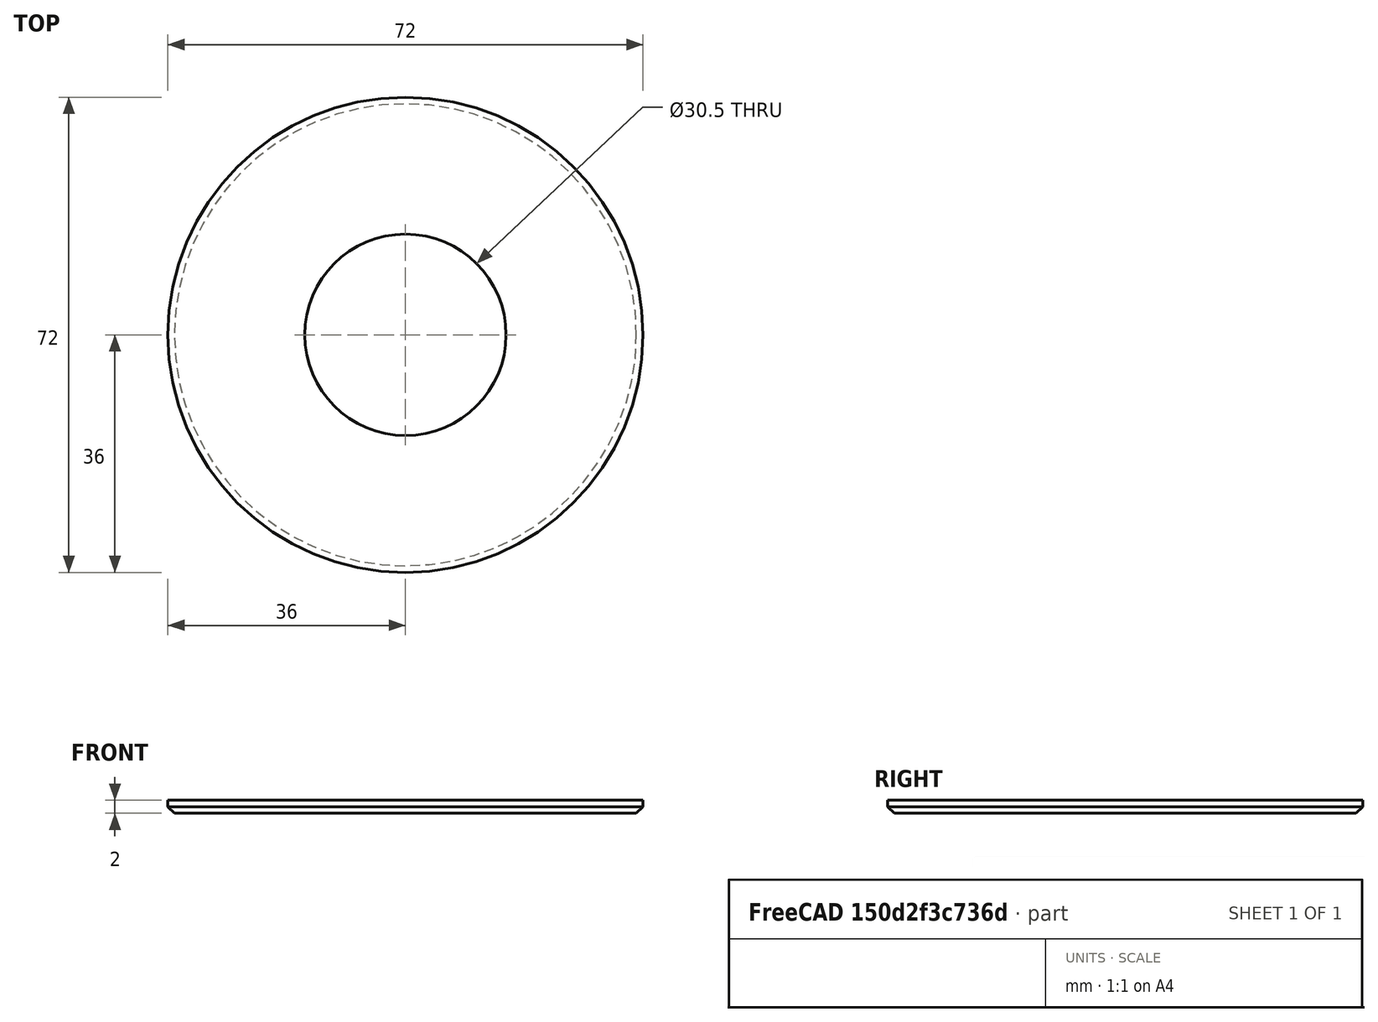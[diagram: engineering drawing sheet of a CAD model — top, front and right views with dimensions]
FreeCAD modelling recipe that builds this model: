
FCSTD DOCUMENT  (FreeCAD 0.18R16146 (Git))
Label: vp4013
License: All rights reserved
LicenseURL: http://en.wikipedia.org/wiki/All_rights_reserved
objects: Sketcher::SketchObject×1, PartDesign::Pad×1, PartDesign::Chamfer×1, PartDesign::Body×1
note: 5 computed .brp shape members not serialized (recipe doc carries the construction recipe); baked Part::Feature solids carry a one-line shape summary decoded from their .brp

FEATURE [Sketcher::SketchObject] Sketch
  MapMode = 5
  Support = -> [XY_Plane]
  sketch-geometry (2):
    g0: Circle CenterX=0 CenterY=0 CenterZ=0 NormalX=0 NormalY=0 NormalZ=1 AngleXU=0 Radius=15.25
    g1: Circle CenterX=0 CenterY=0 CenterZ=0 NormalX=0 NormalY=0 NormalZ=1 AngleXU=0 Radius=36
  constraints (4):
    c: Coincident(g0,g-1)
    c: Coincident(g1,g0)
    c: Diameter(g0) = 30.5
    c: Diameter(g1) = 72
FEATURE [PartDesign::Pad] Pad
  Length = 2
  Length2 = 100
  Profile = -> Sketch
  Type = 0
FEATURE [PartDesign::Chamfer] Chamfer
  Base = -> Pad [Edge2]
  BaseFeature = -> Pad
  Size = 1
FEATURE [PartDesign::Body] Body
  Group = -> [Sketch,Pad,Chamfer]
  Origin = -> Origin
  Tip = -> Chamfer
